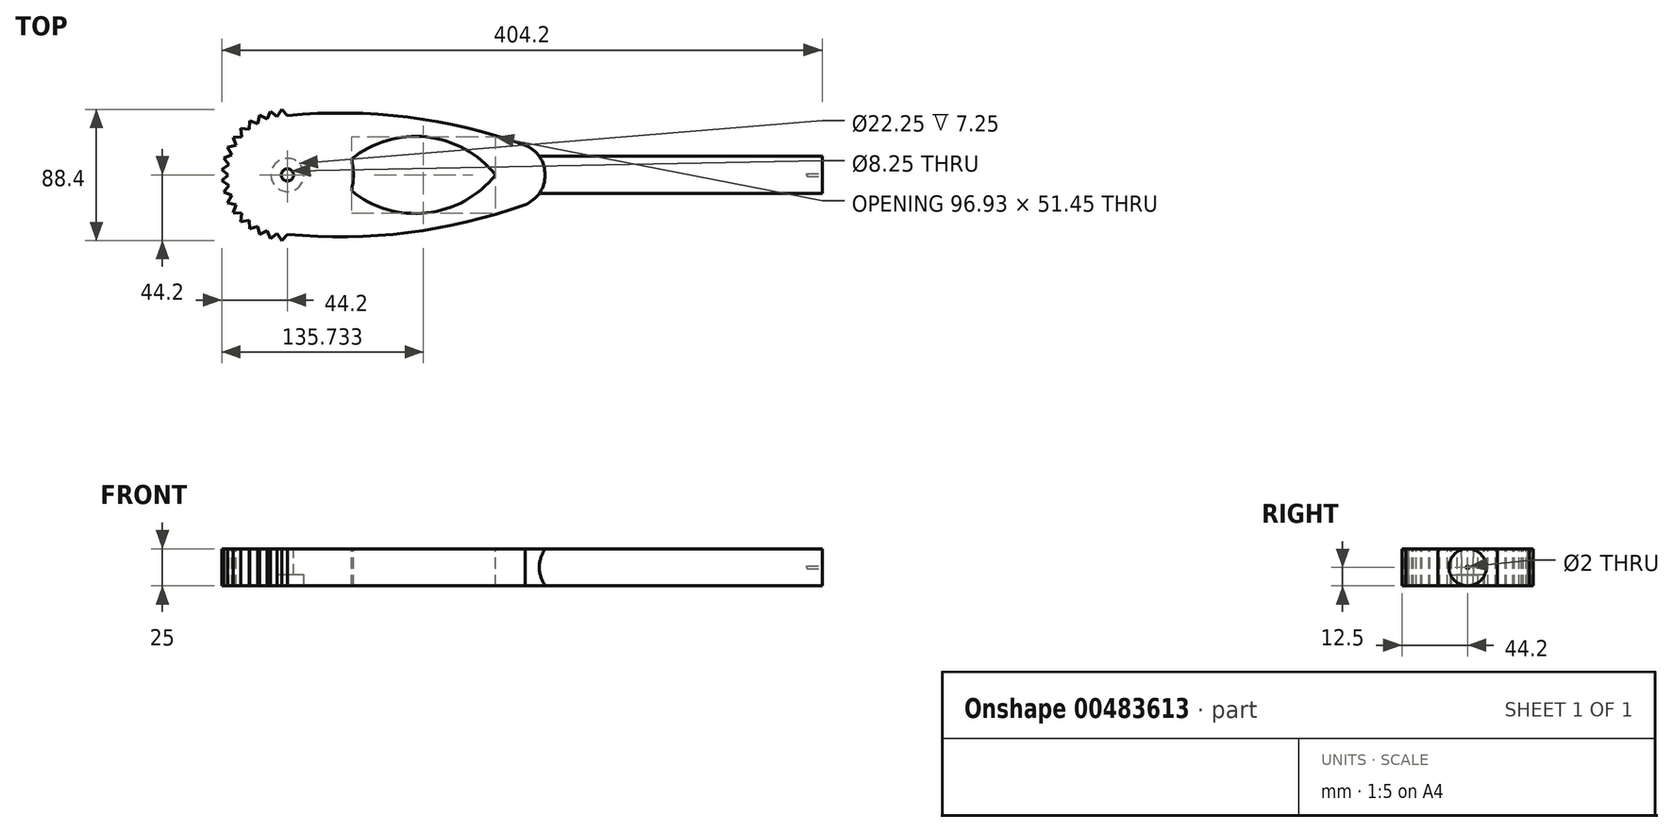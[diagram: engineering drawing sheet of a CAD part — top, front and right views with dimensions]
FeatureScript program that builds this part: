
annotation { "Feature Type Name" : "Feature", "Feature Type Description" : "" }
export const myFeature = defineFeature(function(context is Context, id is Id, definition is map)
    precondition{}
    {
        {
            var Q0;
            Q0=qCreatedBy(makeId("Top.planeOp"),FACE);
            var sketch = newSketch(context, id + "F0", { "sketchPlane" : qUnion([Q0])});
            skLineSegment(sketch, "E0.bottom", {"start": v(200, 12.5) * mm, "end": v(-200, 12.5) * mm});
            skLineSegment(sketch, "E0.top", {"start": v(200, -12.5) * mm, "end": v(-200, -12.5) * mm});
            skLineSegment(sketch, "E0.left", {"start": v(200, 12.5) * mm, "end": v(200, -12.5) * mm});
            skLineSegment(sketch, "E0.right", {"start": v(-200, 12.5) * mm, "end": v(-200, -12.5) * mm});
            skPoint(sketch, "E0.middle", {"position": v(0, 0) * mm});
            skPoint(sketch, "E1", {"position": v(-160, 0) * mm});
            skPoint(sketch, "E1.positionSnap0", {"position": v(-200, 0) * mm});
            skCircle(sketch, "E2", {"center": v(-160, 0) * mm, "radius": 40 * mm});
            skArc(sketch, "E3", {"start": v(0, 20) * mm, "mid": v(-78.9, 38.85) * mm, "end": v(-160, 40) * mm});
            skPoint(sketch, "E3.startSnap0", {"position": v(0, 12.5) * mm});
            skLineSegment(sketch, "E4", {"start": v(-200, 0) * mm, "end": v(200, 0) * mm});
            skArc(sketch, "E5.MirrorCS", {"start": v(0, -20) * mm, "mid": v(-78.9, -38.85) * mm, "end": v(-160, -40) * mm});
            skCircle(sketch, "E6", {"center": v(-8.16, 0) * mm, "radius": 21.6 * mm});
            skPoint(sketch, "E6.third.point", {"position": v(13.44, 0) * mm});
            skSolve(sketch);
        }
        {
            var Q0;
            {var subQ0=sQuery(id+"F0.wireOp",EDGE,"E0.left");Q0=makeQuery(id+"F0.imprint","IMPRINT",FACE,{"disambiguationData":[TD([[makeQuery(id+"F0.imprint","IMPRINT",EDGE,{"derivedFrom":subQ0}),-1.0]])]});}
            var Q1;
            {var subQ0=sQuery(id+"F0.wireOp",EDGE,"E2");var subQ1=sQuery(id+"F0.wireOp",EDGE,"E0.bottom");var subQ7=makeQuery(id+"F0.imprint","INTERSECT",VERTEX,{"disambiguationData":[OD(0.0)],"derivedFrom":[subQ1,subQ0]});Q1=makeQuery(id+"F0.imprint","IMPRINT",FACE,{"disambiguationData":[TD([[makeQuery(id+"F0.imprint","IMPRINT",EDGE,{"disambiguationData":[TD([[subQ7,-1.0]])],"derivedFrom":subQ1}),1.0]])]});}
            var Q2;
            {var subQ0=sQuery(id+"F0.wireOp",EDGE,"E2");var subQ4=sQuery(id+"F0.wireOp",EDGE,"E0.bottom");var subQ5=makeQuery(id+"F0.imprint","INTERSECT",VERTEX,{"disambiguationData":[OD(0.0)],"derivedFrom":[subQ4,subQ0]});Q2=makeQuery(id+"F0.imprint","IMPRINT",FACE,{"disambiguationData":[TD([[makeQuery(id+"F0.imprint","IMPRINT",EDGE,{"disambiguationData":[TD([[subQ5,1.0]])],"derivedFrom":subQ4}),1.0]])]});}
            var Q3;
            {var subQ0=sQuery(id+"F0.wireOp",EDGE,"E2");var subQ1=sQuery(id+"F0.wireOp",EDGE,"E0.bottom");var subQ2=makeQuery(id+"F0.imprint","INTERSECT",VERTEX,{"disambiguationData":[OD(0.0)],"derivedFrom":[subQ1,subQ0]});Q3=makeQuery(id+"F0.imprint","IMPRINT",FACE,{"disambiguationData":[TD([[makeQuery(id+"F0.imprint","IMPRINT",EDGE,{"disambiguationData":[TD([[subQ2,1.0]])],"derivedFrom":subQ1}),-1.0]])]});}
            var Q4;
            {var subQ0=sQuery(id+"F0.wireOp",EDGE,"E2");var subQ1=sQuery(id+"F0.wireOp",EDGE,"E0.top");var subQ2=makeQuery(id+"F0.imprint","INTERSECT",VERTEX,{"disambiguationData":[OD(0.0)],"derivedFrom":[subQ1,subQ0]});Q4=makeQuery(id+"F0.imprint","IMPRINT",FACE,{"disambiguationData":[TD([[makeQuery(id+"F0.imprint","IMPRINT",EDGE,{"disambiguationData":[TD([[subQ2,1.0]])],"derivedFrom":subQ1}),-1.0]])]});}
            var Q5;
            {var subQ0=sQuery(id+"F0.wireOp",EDGE,"E2");var subQ1=sQuery(id+"F0.wireOp",EDGE,"E0.top");var subQ2=makeQuery(id+"F0.imprint","INTERSECT",VERTEX,{"disambiguationData":[OD(0.0)],"derivedFrom":[subQ1,subQ0]});Q5=makeQuery(id+"F0.imprint","IMPRINT",FACE,{"disambiguationData":[TD([[makeQuery(id+"F0.imprint","IMPRINT",EDGE,{"disambiguationData":[TD([[subQ2,1.0]])],"derivedFrom":subQ1}),1.0]])]});}
            var Q6;
            {var subQ0=sQuery(id+"F0.wireOp",EDGE,"E6");var subQ1=sQuery(id+"F0.wireOp",EDGE,"E0.top");var subQ2=makeQuery(id+"F0.imprint","INTERSECT",VERTEX,{"disambiguationData":[OD(1.0)],"derivedFrom":[subQ1,subQ0]});Q6=makeQuery(id+"F0.imprint","IMPRINT",FACE,{"disambiguationData":[TD([[makeQuery(id+"F0.imprint","IMPRINT",EDGE,{"disambiguationData":[TD([[subQ2,-1.0]])],"derivedFrom":subQ1}),1.0]])]});}
            var Q7;
            {var subQ0=sQuery(id+"F0.wireOp",EDGE,"E6");var subQ1=sQuery(id+"F0.wireOp",EDGE,"E0.top");var subQ2=makeQuery(id+"F0.imprint","INTERSECT",VERTEX,{"disambiguationData":[OD(0.0)],"derivedFrom":[subQ1,subQ0]});Q7=makeQuery(id+"F0.imprint","IMPRINT",FACE,{"disambiguationData":[TD([[makeQuery(id+"F0.imprint","IMPRINT",EDGE,{"disambiguationData":[TD([[subQ2,-1.0]])],"derivedFrom":subQ1}),1.0]])]});}
            var Q8;
            {var subQ0=sQuery(id+"F0.wireOp",EDGE,"E6");var subQ1=sQuery(id+"F0.wireOp",EDGE,"E0.top");var subQ2=makeQuery(id+"F0.imprint","INTERSECT",VERTEX,{"disambiguationData":[OD(0.0)],"derivedFrom":[subQ1,subQ0]});Q8=makeQuery(id+"F0.imprint","IMPRINT",FACE,{"disambiguationData":[TD([[makeQuery(id+"F0.imprint","IMPRINT",EDGE,{"disambiguationData":[TD([[subQ2,-1.0]])],"derivedFrom":subQ1}),-1.0]])]});}
            var Q9;
            {var subQ0=sQuery(id+"F0.wireOp",EDGE,"E6");var subQ1=sQuery(id+"F0.wireOp",EDGE,"E0.top");var subQ2=makeQuery(id+"F0.imprint","INTERSECT",VERTEX,{"disambiguationData":[OD(1.0)],"derivedFrom":[subQ1,subQ0]});Q9=makeQuery(id+"F0.imprint","IMPRINT",FACE,{"disambiguationData":[TD([[makeQuery(id+"F0.imprint","IMPRINT",EDGE,{"disambiguationData":[TD([[subQ2,-1.0]])],"derivedFrom":subQ1}),-1.0]])]});}
            var Q10;
            {var subQ0=sQuery(id+"F0.wireOp",EDGE,"E6");var subQ1=sQuery(id+"F0.wireOp",EDGE,"E0.bottom");var subQ2=makeQuery(id+"F0.imprint","INTERSECT",VERTEX,{"disambiguationData":[OD(1.0)],"derivedFrom":[subQ1,subQ0]});Q10=makeQuery(id+"F0.imprint","IMPRINT",FACE,{"disambiguationData":[TD([[makeQuery(id+"F0.imprint","IMPRINT",EDGE,{"disambiguationData":[TD([[subQ2,-1.0]])],"derivedFrom":subQ1}),1.0]])]});}
            var Q11;
            {var subQ0=sQuery(id+"F0.wireOp",EDGE,"E6");var subQ1=sQuery(id+"F0.wireOp",EDGE,"E0.bottom");var subQ2=makeQuery(id+"F0.imprint","INTERSECT",VERTEX,{"disambiguationData":[OD(0.0)],"derivedFrom":[subQ1,subQ0]});Q11=makeQuery(id+"F0.imprint","IMPRINT",FACE,{"disambiguationData":[TD([[makeQuery(id+"F0.imprint","IMPRINT",EDGE,{"disambiguationData":[TD([[subQ2,-1.0]])],"derivedFrom":subQ1}),1.0]])]});}
            var Q12;
            {var subQ0=sQuery(id+"F0.wireOp",EDGE,"E6");var subQ1=sQuery(id+"F0.wireOp",EDGE,"E0.bottom");var subQ2=makeQuery(id+"F0.imprint","INTERSECT",VERTEX,{"disambiguationData":[OD(0.0)],"derivedFrom":[subQ1,subQ0]});Q12=makeQuery(id+"F0.imprint","IMPRINT",FACE,{"disambiguationData":[TD([[makeQuery(id+"F0.imprint","IMPRINT",EDGE,{"disambiguationData":[TD([[subQ2,-1.0]])],"derivedFrom":subQ1}),-1.0]])]});}
            var Q13;
            {var subQ0=sQuery(id+"F0.wireOp",EDGE,"E6");var subQ1=sQuery(id+"F0.wireOp",EDGE,"E0.bottom");var subQ2=makeQuery(id+"F0.imprint","INTERSECT",VERTEX,{"disambiguationData":[OD(1.0)],"derivedFrom":[subQ1,subQ0]});Q13=makeQuery(id+"F0.imprint","IMPRINT",FACE,{"disambiguationData":[TD([[makeQuery(id+"F0.imprint","IMPRINT",EDGE,{"disambiguationData":[TD([[subQ2,-1.0]])],"derivedFrom":subQ1}),-1.0]])]});}
            extrude(context, id + "F1", {"entities" : qUnion([Q0, Q1, Q2, Q3, Q4, Q5, Q6, Q7, Q8, Q9, Q10, Q11, Q12, Q13]), "depth" : 25 * mm});
        }
        {
            var Q0;
            Q0=makeQuery(id+"F1.opExtrude","CAP_EDGE",EDGE,{"disambiguationData":[OSD([sQuery(id+"F0.wireOp",EDGE,"E0.top")])],"isStart":false});
            var Q1;
            Q1=makeQuery(id+"F1.opExtrude","CAP_EDGE",EDGE,{"disambiguationData":[OSD([sQuery(id+"F0.wireOp",EDGE,"E0.bottom")])],"isStart":false});
            var Q2;
            Q2=makeQuery(id+"F1.opExtrude","CAP_EDGE",EDGE,{"disambiguationData":[OSD([sQuery(id+"F0.wireOp",EDGE,"E0.bottom")])],"isStart":true});
            var Q3;
            Q3=makeQuery(id+"F1.opExtrude","CAP_EDGE",EDGE,{"disambiguationData":[OSD([sQuery(id+"F0.wireOp",EDGE,"E0.top")])],"isStart":true});
            fillet(context, id + "F2", {"entities" : qUnion([Q0, Q1, Q2, Q3]), "radius" : 12.5 * mm, "tangentPropagation" : true, "allowEdgeOverflow" : false});
        }
        {
            var Q0;
            Q0=makeQuery(id+"F1.opExtrude","CAP_FACE",FACE,{"disambiguationData":[OSD([sQuery(id+"F0.wireOp",EDGE,"E0.bottom"),sQuery(id+"F0.wireOp",EDGE,"E0.top"),sQuery(id+"F0.wireOp",EDGE,"E0.left"),sQuery(id+"F0.wireOp",EDGE,"E0.right"),sQuery(id+"F0.wireOp",EDGE,"E2"),sQuery(id+"F0.wireOp",EDGE,"E3"),sQuery(id+"F0.wireOp",EDGE,"E5.MirrorCS"),sQuery(id+"F0.wireOp",EDGE,"E6")])],"isStart":false});
            var sketch = newSketch(context, id + "F3", { "sketchPlane" : qUnion([Q0])});
            skCircle(sketch, "E7", {"center": v(-160, 0) * mm, "radius": 40 * mm});
            skLineSegment(sketch, "E8", {"start": v(-160, 40) * mm, "end": v(-148.02, 53.01) * mm});
            skLineSegment(sketch, "E9", {"start": v(-171.98, 53.01) * mm, "end": v(-160, 40) * mm});
            skLineSegment(sketch, "E10.1.0", {"start": v(-166.95, 39.4) * mm, "end": v(-157.41, 54.29) * mm});
            skLineSegment(sketch, "E10.1.1", {"start": v(-181, 50.13) * mm, "end": v(-166.95, 39.4) * mm});
            skLineSegment(sketch, "E10.2.0", {"start": v(-173.68, 37.59) * mm, "end": v(-166.88, 53.91) * mm});
            skLineSegment(sketch, "E10.2.1", {"start": v(-189.38, 45.72) * mm, "end": v(-173.68, 37.59) * mm});
            skLineSegment(sketch, "E10.3.0", {"start": v(-180, 34.64) * mm, "end": v(-176.14, 51.9) * mm});
            skLineSegment(sketch, "E10.3.1", {"start": v(-196.88, 39.92) * mm, "end": v(-180, 34.64) * mm});
            skLineSegment(sketch, "E10.4.0", {"start": v(-185.71, 30.64) * mm, "end": v(-184.9, 48.3) * mm});
            skLineSegment(sketch, "E10.4.1", {"start": v(-203.25, 32.91) * mm, "end": v(-185.71, 30.64) * mm});
            skLineSegment(sketch, "E10.5.0", {"start": v(-190.64, 25.71) * mm, "end": v(-192.91, 43.25) * mm});
            skLineSegment(sketch, "E10.5.1", {"start": v(-208.3, 24.9) * mm, "end": v(-190.64, 25.71) * mm});
            skLineSegment(sketch, "E10.6.0", {"start": v(-194.64, 20) * mm, "end": v(-199.92, 36.88) * mm});
            skLineSegment(sketch, "E10.6.1", {"start": v(-211.9, 16.14) * mm, "end": v(-194.64, 20) * mm});
            skLineSegment(sketch, "E10.7.0", {"start": v(-197.59, 13.68) * mm, "end": v(-205.72, 29.38) * mm});
            skLineSegment(sketch, "E10.7.1", {"start": v(-213.91, 6.88) * mm, "end": v(-197.59, 13.68) * mm});
            skLineSegment(sketch, "E10.8.0", {"start": v(-199.4, 6.95) * mm, "end": v(-210.13, 21) * mm});
            skLineSegment(sketch, "E10.8.1", {"start": v(-214.29, -2.59) * mm, "end": v(-199.4, 6.95) * mm});
            skLineSegment(sketch, "E10.9.0", {"start": v(-200, 0) * mm, "end": v(-213.01, 11.98) * mm});
            skLineSegment(sketch, "E10.9.1", {"start": v(-213.01, -11.98) * mm, "end": v(-200, 0) * mm});
            skLineSegment(sketch, "E10.10.0", {"start": v(-199.4, -6.95) * mm, "end": v(-214.29, 2.59) * mm});
            skLineSegment(sketch, "E10.10.1", {"start": v(-210.13, -21) * mm, "end": v(-199.4, -6.95) * mm});
            skLineSegment(sketch, "E10.11.0", {"start": v(-197.59, -13.68) * mm, "end": v(-213.91, -6.88) * mm});
            skLineSegment(sketch, "E10.11.1", {"start": v(-205.72, -29.38) * mm, "end": v(-197.59, -13.68) * mm});
            skLineSegment(sketch, "E10.12.0", {"start": v(-194.64, -20) * mm, "end": v(-211.9, -16.14) * mm});
            skLineSegment(sketch, "E10.12.1", {"start": v(-199.92, -36.88) * mm, "end": v(-194.64, -20) * mm});
            skLineSegment(sketch, "E10.13.0", {"start": v(-190.64, -25.71) * mm, "end": v(-208.3, -24.9) * mm});
            skLineSegment(sketch, "E10.13.1", {"start": v(-192.91, -43.25) * mm, "end": v(-190.64, -25.71) * mm});
            skLineSegment(sketch, "E10.14.0", {"start": v(-185.71, -30.64) * mm, "end": v(-203.25, -32.91) * mm});
            skLineSegment(sketch, "E10.14.1", {"start": v(-184.9, -48.3) * mm, "end": v(-185.71, -30.64) * mm});
            skLineSegment(sketch, "E10.15.0", {"start": v(-180, -34.64) * mm, "end": v(-196.88, -39.92) * mm});
            skLineSegment(sketch, "E10.15.1", {"start": v(-176.14, -51.9) * mm, "end": v(-180, -34.64) * mm});
            skLineSegment(sketch, "E10.16.0", {"start": v(-173.68, -37.59) * mm, "end": v(-189.38, -45.72) * mm});
            skLineSegment(sketch, "E10.16.1", {"start": v(-166.88, -53.91) * mm, "end": v(-173.68, -37.59) * mm});
            skLineSegment(sketch, "E10.17.0", {"start": v(-166.95, -39.4) * mm, "end": v(-181, -50.13) * mm});
            skLineSegment(sketch, "E10.17.1", {"start": v(-157.41, -54.29) * mm, "end": v(-166.95, -39.4) * mm});
            skLineSegment(sketch, "E10.18.0", {"start": v(-160, -40) * mm, "end": v(-171.98, -53.01) * mm});
            skLineSegment(sketch, "E10.18.1", {"start": v(-148.02, -53.01) * mm, "end": v(-160, -40) * mm});
            skLineSegment(sketch, "E10.19.0", {"start": v(-153.05, -39.4) * mm, "end": v(-162.59, -54.29) * mm});
            skLineSegment(sketch, "E10.19.1", {"start": v(-139, -50.13) * mm, "end": v(-153.05, -39.4) * mm});
            skLineSegment(sketch, "E10.20.0", {"start": v(-146.32, -37.59) * mm, "end": v(-153.12, -53.91) * mm});
            skLineSegment(sketch, "E10.20.1", {"start": v(-130.62, -45.72) * mm, "end": v(-146.32, -37.59) * mm});
            skLineSegment(sketch, "E10.21.0", {"start": v(-140, -34.64) * mm, "end": v(-143.86, -51.9) * mm});
            skLineSegment(sketch, "E10.21.1", {"start": v(-123.12, -39.92) * mm, "end": v(-140, -34.64) * mm});
            skLineSegment(sketch, "E10.22.0", {"start": v(-134.29, -30.64) * mm, "end": v(-135.1, -48.3) * mm});
            skLineSegment(sketch, "E10.22.1", {"start": v(-116.75, -32.91) * mm, "end": v(-134.29, -30.64) * mm});
            skLineSegment(sketch, "E10.23.0", {"start": v(-129.36, -25.71) * mm, "end": v(-127.09, -43.25) * mm});
            skLineSegment(sketch, "E10.23.1", {"start": v(-111.7, -24.9) * mm, "end": v(-129.36, -25.71) * mm});
            skLineSegment(sketch, "E10.24.0", {"start": v(-125.36, -20) * mm, "end": v(-120.08, -36.88) * mm});
            skLineSegment(sketch, "E10.24.1", {"start": v(-108.1, -16.14) * mm, "end": v(-125.36, -20) * mm});
            skLineSegment(sketch, "E10.25.0", {"start": v(-122.41, -13.68) * mm, "end": v(-114.28, -29.38) * mm});
            skLineSegment(sketch, "E10.25.1", {"start": v(-106.09, -6.88) * mm, "end": v(-122.41, -13.68) * mm});
            skLineSegment(sketch, "E10.26.0", {"start": v(-120.6, -6.95) * mm, "end": v(-109.87, -21) * mm});
            skLineSegment(sketch, "E10.26.1", {"start": v(-105.71, 2.59) * mm, "end": v(-120.6, -6.95) * mm});
            skLineSegment(sketch, "E10.27.0", {"start": v(-120, 0) * mm, "end": v(-106.99, -11.98) * mm});
            skLineSegment(sketch, "E10.27.1", {"start": v(-106.99, 11.98) * mm, "end": v(-120, 0) * mm});
            skLineSegment(sketch, "E10.28.0", {"start": v(-120.6, 6.95) * mm, "end": v(-105.71, -2.59) * mm});
            skLineSegment(sketch, "E10.28.1", {"start": v(-109.87, 21) * mm, "end": v(-120.6, 6.95) * mm});
            skLineSegment(sketch, "E10.29.0", {"start": v(-122.41, 13.68) * mm, "end": v(-106.09, 6.88) * mm});
            skLineSegment(sketch, "E10.29.1", {"start": v(-114.28, 29.38) * mm, "end": v(-122.41, 13.68) * mm});
            skLineSegment(sketch, "E10.30.0", {"start": v(-125.36, 20) * mm, "end": v(-108.1, 16.14) * mm});
            skLineSegment(sketch, "E10.30.1", {"start": v(-120.08, 36.88) * mm, "end": v(-125.36, 20) * mm});
            skLineSegment(sketch, "E10.31.0", {"start": v(-129.36, 25.71) * mm, "end": v(-111.7, 24.9) * mm});
            skLineSegment(sketch, "E10.31.1", {"start": v(-127.09, 43.25) * mm, "end": v(-129.36, 25.71) * mm});
            skLineSegment(sketch, "E10.32.0", {"start": v(-134.29, 30.64) * mm, "end": v(-116.75, 32.91) * mm});
            skLineSegment(sketch, "E10.32.1", {"start": v(-135.1, 48.3) * mm, "end": v(-134.29, 30.64) * mm});
            skLineSegment(sketch, "E10.33.0", {"start": v(-140, 34.64) * mm, "end": v(-123.12, 39.92) * mm});
            skLineSegment(sketch, "E10.33.1", {"start": v(-143.86, 51.9) * mm, "end": v(-140, 34.64) * mm});
            skLineSegment(sketch, "E10.34.0", {"start": v(-146.32, 37.59) * mm, "end": v(-130.62, 45.72) * mm});
            skLineSegment(sketch, "E10.34.1", {"start": v(-153.12, 53.91) * mm, "end": v(-146.32, 37.59) * mm});
            skLineSegment(sketch, "E10.35.0", {"start": v(-153.05, 39.4) * mm, "end": v(-139, 50.13) * mm});
            skLineSegment(sketch, "E10.35.1", {"start": v(-162.59, 54.29) * mm, "end": v(-153.05, 39.4) * mm});
            skArc(sketch, "E11", {"start": v(-160, 70.8) * mm, "mid": v(-230.8, 0) * mm, "end": v(-160, -70.8) * mm});
            skLineSegment(sketch, "E12", {"start": v(-160, 70.8) * mm, "end": v(-160, -70.8) * mm});
            skPoint(sketch, "E13.orphan", {"position": v(-160, 103.77) * mm});
            skSolve(sketch);
        }
        {
            var Q0;
            {var subQ8=sQuery(id+"F3.wireOp",EDGE,"E12");var subQ17=sQuery(id+"F3.wireOp",EDGE,"E11");var subQ18=makeQuery(id+"F3.imprint","INTERSECT",VERTEX,{"disambiguationData":[OD(0.0)],"derivedFrom":[subQ17,subQ8]});Q0=makeQuery(id+"F3.imprint","IMPRINT",FACE,{"disambiguationData":[TD([[makeQuery(id+"F3.imprint","IMPRINT",EDGE,{"disambiguationData":[TD([[subQ18,-1.0]])],"derivedFrom":subQ17}),1.0]])]});}
            var Q1;
            {var subQ0=sQuery(id+"F3.wireOp",EDGE,"E10.7.1");var subQ3=sQuery(id+"F3.wireOp",EDGE,"E10.8.0");var subQ5=makeQuery(id+"F3.imprint","INTERSECT",VERTEX,{"derivedFrom":[subQ0,subQ3]});Q1=makeQuery(id+"F3.imprint","IMPRINT",FACE,{"disambiguationData":[TD([[makeQuery(id+"F3.imprint","IMPRINT",EDGE,{"disambiguationData":[TD([[subQ5,-1.0]])],"derivedFrom":subQ0}),-1.0]])]});}
            var Q2;
            {var subQ0=sQuery(id+"F3.wireOp",EDGE,"E10.9.0");var subQ3=sQuery(id+"F3.wireOp",EDGE,"E10.8.1");var subQ5=makeQuery(id+"F3.imprint","INTERSECT",VERTEX,{"derivedFrom":[subQ3,subQ0]});Q2=makeQuery(id+"F3.imprint","IMPRINT",FACE,{"disambiguationData":[TD([[makeQuery(id+"F3.imprint","IMPRINT",EDGE,{"disambiguationData":[TD([[subQ5,-1.0]])],"derivedFrom":subQ3}),-1.0]])]});}
            var Q3;
            {var subQ0=sQuery(id+"F3.wireOp",EDGE,"E10.9.1");var subQ3=sQuery(id+"F3.wireOp",EDGE,"E10.10.0");var subQ5=makeQuery(id+"F3.imprint","INTERSECT",VERTEX,{"derivedFrom":[subQ0,subQ3]});Q3=makeQuery(id+"F3.imprint","IMPRINT",FACE,{"disambiguationData":[TD([[makeQuery(id+"F3.imprint","IMPRINT",EDGE,{"disambiguationData":[TD([[subQ5,-1.0]])],"derivedFrom":subQ0}),-1.0]])]});}
            var Q4;
            {var subQ0=sQuery(id+"F3.wireOp",EDGE,"E10.10.1");var subQ3=sQuery(id+"F3.wireOp",EDGE,"E10.11.0");var subQ5=makeQuery(id+"F3.imprint","INTERSECT",VERTEX,{"derivedFrom":[subQ0,subQ3]});Q4=makeQuery(id+"F3.imprint","IMPRINT",FACE,{"disambiguationData":[TD([[makeQuery(id+"F3.imprint","IMPRINT",EDGE,{"disambiguationData":[TD([[subQ5,-1.0]])],"derivedFrom":subQ0}),-1.0]])]});}
            var Q5;
            {var subQ0=sQuery(id+"F3.wireOp",EDGE,"E10.8.0");var subQ1=sQuery(id+"F3.wireOp",EDGE,"E10.6.1");var subQ2=makeQuery(id+"F3.imprint","INTERSECT",VERTEX,{"derivedFrom":[subQ1,subQ0]});Q5=makeQuery(id+"F3.imprint","IMPRINT",FACE,{"disambiguationData":[TD([[makeQuery(id+"F3.imprint","IMPRINT",EDGE,{"disambiguationData":[TD([[subQ2,-1.0]])],"derivedFrom":subQ1}),-1.0]])]});}
            var Q6;
            {var subQ0=sQuery(id+"F3.wireOp",EDGE,"E10.9.0");var subQ1=sQuery(id+"F3.wireOp",EDGE,"E10.7.1");var subQ2=makeQuery(id+"F3.imprint","INTERSECT",VERTEX,{"derivedFrom":[subQ1,subQ0]});Q6=makeQuery(id+"F3.imprint","IMPRINT",FACE,{"disambiguationData":[TD([[makeQuery(id+"F3.imprint","IMPRINT",EDGE,{"disambiguationData":[TD([[subQ2,-1.0]])],"derivedFrom":subQ1}),-1.0]])]});}
            var Q7;
            {var subQ0=sQuery(id+"F3.wireOp",EDGE,"E10.6.1");var subQ3=sQuery(id+"F3.wireOp",EDGE,"E10.7.0");var subQ5=makeQuery(id+"F3.imprint","INTERSECT",VERTEX,{"derivedFrom":[subQ0,subQ3]});Q7=makeQuery(id+"F3.imprint","IMPRINT",FACE,{"disambiguationData":[TD([[makeQuery(id+"F3.imprint","IMPRINT",EDGE,{"disambiguationData":[TD([[subQ5,-1.0]])],"derivedFrom":subQ0}),-1.0]])]});}
            var Q8;
            {var subQ0=sQuery(id+"F3.wireOp",EDGE,"E10.11.1");var subQ3=sQuery(id+"F3.wireOp",EDGE,"E10.12.0");var subQ5=makeQuery(id+"F3.imprint","INTERSECT",VERTEX,{"derivedFrom":[subQ0,subQ3]});Q8=makeQuery(id+"F3.imprint","IMPRINT",FACE,{"disambiguationData":[TD([[makeQuery(id+"F3.imprint","IMPRINT",EDGE,{"disambiguationData":[TD([[subQ5,-1.0]])],"derivedFrom":subQ0}),-1.0]])]});}
            extrude(context, id + "F4", {"entities" : qUnion([Q0, Q1, Q2, Q3, Q4, Q5, Q6, Q7, Q8]), "operationType" : NewBodyOperationType.REMOVE, "endBound" : BoundingType.THROUGH_ALL, "oppositeDirection" : true, "depth" : 25 * mm});
        }
        {
            var Q0;
            Q0=makeQuery(id+"F1.opExtrude","CAP_FACE",FACE,{"disambiguationData":[OSD([sQuery(id+"F0.wireOp",EDGE,"E0.bottom"),sQuery(id+"F0.wireOp",EDGE,"E0.top"),sQuery(id+"F0.wireOp",EDGE,"E0.left"),sQuery(id+"F0.wireOp",EDGE,"E0.right"),sQuery(id+"F0.wireOp",EDGE,"E2"),sQuery(id+"F0.wireOp",EDGE,"E3"),sQuery(id+"F0.wireOp",EDGE,"E5.MirrorCS"),sQuery(id+"F0.wireOp",EDGE,"E6")])],"isStart":false});
            var sketch = newSketch(context, id + "F5", { "sketchPlane" : qUnion([Q0])});
            skCircle(sketch, "E14", {"center": v(-160, 0) * mm, "radius": 4.12 * mm});
            skCircle(sketch, "E15", {"center": v(-160, 0) * mm, "radius": 11.12 * mm});
            skSolve(sketch);
        }
        {
            var Q0;
            Q0=makeQuery(id+"F5.imprint","IMPRINT",FACE,{"disambiguationData":[TD([[makeQuery(id+"F5.imprint","IMPRINT",EDGE,{"derivedFrom":sQuery(id+"F5.wireOp",EDGE,"E14")}),-1.0]])]});
            var Q1;
            Q1=makeQuery(id+"F5.imprint","IMPRINT",FACE,{"disambiguationData":[TD([[makeQuery(id+"F5.imprint","IMPRINT",EDGE,{"derivedFrom":sQuery(id+"F5.wireOp",EDGE,"E14")}),1.0]])]});
            extrude(context, id + "F6", {"entities" : qUnion([Q0, Q1]), "operationType" : NewBodyOperationType.REMOVE, "oppositeDirection" : true, "depth" : 25 * mm});
        }
        {
            var Q0;
            {var subQ0=sQuery(id+"F3.wireOp",EDGE,"E9");var subQ3=sQuery(id+"F3.wireOp",EDGE,"E10.1.0");var subQ5=makeQuery(id+"F3.imprint","INTERSECT",VERTEX,{"derivedFrom":[subQ0,subQ3]});Q0=makeQuery(id+"F3.imprint","IMPRINT",FACE,{"disambiguationData":[TD([[makeQuery(id+"F3.imprint","IMPRINT",EDGE,{"disambiguationData":[TD([[subQ5,1.0]])],"derivedFrom":subQ3}),-1.0]])]});}
            var Q1;
            {var subQ0=sQuery(id+"F3.wireOp",EDGE,"E10.1.1");var subQ3=sQuery(id+"F3.wireOp",EDGE,"E10.2.0");var subQ5=makeQuery(id+"F3.imprint","INTERSECT",VERTEX,{"derivedFrom":[subQ0,subQ3]});Q1=makeQuery(id+"F3.imprint","IMPRINT",FACE,{"disambiguationData":[TD([[makeQuery(id+"F3.imprint","IMPRINT",EDGE,{"disambiguationData":[TD([[subQ5,-1.0]])],"derivedFrom":subQ0}),-1.0]])]});}
            var Q2;
            {var subQ0=sQuery(id+"F3.wireOp",EDGE,"E10.2.1");var subQ3=sQuery(id+"F3.wireOp",EDGE,"E10.3.0");var subQ5=makeQuery(id+"F3.imprint","INTERSECT",VERTEX,{"derivedFrom":[subQ0,subQ3]});Q2=makeQuery(id+"F3.imprint","IMPRINT",FACE,{"disambiguationData":[TD([[makeQuery(id+"F3.imprint","IMPRINT",EDGE,{"disambiguationData":[TD([[subQ5,-1.0]])],"derivedFrom":subQ0}),-1.0]])]});}
            var Q3;
            {var subQ0=sQuery(id+"F3.wireOp",EDGE,"E10.3.1");var subQ3=sQuery(id+"F3.wireOp",EDGE,"E10.4.0");var subQ5=makeQuery(id+"F3.imprint","INTERSECT",VERTEX,{"derivedFrom":[subQ0,subQ3]});Q3=makeQuery(id+"F3.imprint","IMPRINT",FACE,{"disambiguationData":[TD([[makeQuery(id+"F3.imprint","IMPRINT",EDGE,{"disambiguationData":[TD([[subQ5,-1.0]])],"derivedFrom":subQ0}),-1.0]])]});}
            var Q4;
            {var subQ0=sQuery(id+"F3.wireOp",EDGE,"E10.4.1");var subQ3=sQuery(id+"F3.wireOp",EDGE,"E10.5.0");var subQ5=makeQuery(id+"F3.imprint","INTERSECT",VERTEX,{"derivedFrom":[subQ0,subQ3]});Q4=makeQuery(id+"F3.imprint","IMPRINT",FACE,{"disambiguationData":[TD([[makeQuery(id+"F3.imprint","IMPRINT",EDGE,{"disambiguationData":[TD([[subQ5,-1.0]])],"derivedFrom":subQ0}),-1.0]])]});}
            var Q5;
            {var subQ0=sQuery(id+"F3.wireOp",EDGE,"E10.5.1");var subQ3=sQuery(id+"F3.wireOp",EDGE,"E10.6.0");var subQ5=makeQuery(id+"F3.imprint","INTERSECT",VERTEX,{"derivedFrom":[subQ0,subQ3]});Q5=makeQuery(id+"F3.imprint","IMPRINT",FACE,{"disambiguationData":[TD([[makeQuery(id+"F3.imprint","IMPRINT",EDGE,{"disambiguationData":[TD([[subQ5,-1.0]])],"derivedFrom":subQ0}),-1.0]])]});}
            var Q6;
            {var subQ0=sQuery(id+"F3.wireOp",EDGE,"E10.6.1");var subQ3=sQuery(id+"F3.wireOp",EDGE,"E10.7.0");var subQ5=makeQuery(id+"F3.imprint","INTERSECT",VERTEX,{"derivedFrom":[subQ0,subQ3]});Q6=makeQuery(id+"F3.imprint","IMPRINT",FACE,{"disambiguationData":[TD([[makeQuery(id+"F3.imprint","IMPRINT",EDGE,{"disambiguationData":[TD([[subQ5,-1.0]])],"derivedFrom":subQ0}),-1.0]])]});}
            var Q7;
            {var subQ0=sQuery(id+"F3.wireOp",EDGE,"E10.7.1");var subQ3=sQuery(id+"F3.wireOp",EDGE,"E10.8.0");var subQ5=makeQuery(id+"F3.imprint","INTERSECT",VERTEX,{"derivedFrom":[subQ0,subQ3]});Q7=makeQuery(id+"F3.imprint","IMPRINT",FACE,{"disambiguationData":[TD([[makeQuery(id+"F3.imprint","IMPRINT",EDGE,{"disambiguationData":[TD([[subQ5,-1.0]])],"derivedFrom":subQ0}),-1.0]])]});}
            var Q8;
            {var subQ0=sQuery(id+"F3.wireOp",EDGE,"E10.9.0");var subQ3=sQuery(id+"F3.wireOp",EDGE,"E10.8.1");var subQ5=makeQuery(id+"F3.imprint","INTERSECT",VERTEX,{"derivedFrom":[subQ3,subQ0]});Q8=makeQuery(id+"F3.imprint","IMPRINT",FACE,{"disambiguationData":[TD([[makeQuery(id+"F3.imprint","IMPRINT",EDGE,{"disambiguationData":[TD([[subQ5,-1.0]])],"derivedFrom":subQ3}),-1.0]])]});}
            var Q9;
            {var subQ0=sQuery(id+"F3.wireOp",EDGE,"E10.9.1");var subQ3=sQuery(id+"F3.wireOp",EDGE,"E10.10.0");var subQ5=makeQuery(id+"F3.imprint","INTERSECT",VERTEX,{"derivedFrom":[subQ0,subQ3]});Q9=makeQuery(id+"F3.imprint","IMPRINT",FACE,{"disambiguationData":[TD([[makeQuery(id+"F3.imprint","IMPRINT",EDGE,{"disambiguationData":[TD([[subQ5,-1.0]])],"derivedFrom":subQ0}),-1.0]])]});}
            var Q10;
            {var subQ0=sQuery(id+"F3.wireOp",EDGE,"E10.10.1");var subQ3=sQuery(id+"F3.wireOp",EDGE,"E10.11.0");var subQ5=makeQuery(id+"F3.imprint","INTERSECT",VERTEX,{"derivedFrom":[subQ0,subQ3]});Q10=makeQuery(id+"F3.imprint","IMPRINT",FACE,{"disambiguationData":[TD([[makeQuery(id+"F3.imprint","IMPRINT",EDGE,{"disambiguationData":[TD([[subQ5,-1.0]])],"derivedFrom":subQ0}),-1.0]])]});}
            var Q11;
            {var subQ0=sQuery(id+"F3.wireOp",EDGE,"E10.13.1");var subQ3=sQuery(id+"F3.wireOp",EDGE,"E10.14.0");var subQ5=makeQuery(id+"F3.imprint","INTERSECT",VERTEX,{"derivedFrom":[subQ0,subQ3]});Q11=makeQuery(id+"F3.imprint","IMPRINT",FACE,{"disambiguationData":[TD([[makeQuery(id+"F3.imprint","IMPRINT",EDGE,{"disambiguationData":[TD([[subQ5,-1.0]])],"derivedFrom":subQ0}),-1.0]])]});}
            var Q12;
            {var subQ0=sQuery(id+"F3.wireOp",EDGE,"E10.14.1");var subQ3=sQuery(id+"F3.wireOp",EDGE,"E10.15.0");var subQ5=makeQuery(id+"F3.imprint","INTERSECT",VERTEX,{"derivedFrom":[subQ0,subQ3]});Q12=makeQuery(id+"F3.imprint","IMPRINT",FACE,{"disambiguationData":[TD([[makeQuery(id+"F3.imprint","IMPRINT",EDGE,{"disambiguationData":[TD([[subQ5,-1.0]])],"derivedFrom":subQ0}),-1.0]])]});}
            var Q13;
            {var subQ0=sQuery(id+"F3.wireOp",EDGE,"E10.15.1");var subQ3=sQuery(id+"F3.wireOp",EDGE,"E10.16.0");var subQ5=makeQuery(id+"F3.imprint","INTERSECT",VERTEX,{"derivedFrom":[subQ0,subQ3]});Q13=makeQuery(id+"F3.imprint","IMPRINT",FACE,{"disambiguationData":[TD([[makeQuery(id+"F3.imprint","IMPRINT",EDGE,{"disambiguationData":[TD([[subQ5,-1.0]])],"derivedFrom":subQ0}),-1.0]])]});}
            var Q14;
            {var subQ0=sQuery(id+"F3.wireOp",EDGE,"E10.12.1");var subQ3=sQuery(id+"F3.wireOp",EDGE,"E10.13.0");var subQ5=makeQuery(id+"F3.imprint","INTERSECT",VERTEX,{"derivedFrom":[subQ0,subQ3]});Q14=makeQuery(id+"F3.imprint","IMPRINT",FACE,{"disambiguationData":[TD([[makeQuery(id+"F3.imprint","IMPRINT",EDGE,{"disambiguationData":[TD([[subQ5,-1.0]])],"derivedFrom":subQ0}),-1.0]])]});}
            var Q15;
            {var subQ0=sQuery(id+"F3.wireOp",EDGE,"E10.11.1");var subQ3=sQuery(id+"F3.wireOp",EDGE,"E10.12.0");var subQ5=makeQuery(id+"F3.imprint","INTERSECT",VERTEX,{"derivedFrom":[subQ0,subQ3]});Q15=makeQuery(id+"F3.imprint","IMPRINT",FACE,{"disambiguationData":[TD([[makeQuery(id+"F3.imprint","IMPRINT",EDGE,{"disambiguationData":[TD([[subQ5,-1.0]])],"derivedFrom":subQ0}),-1.0]])]});}
            var Q16;
            {var subQ0=sQuery(id+"F3.wireOp",EDGE,"E10.16.1");var subQ3=sQuery(id+"F3.wireOp",EDGE,"E10.17.0");var subQ5=makeQuery(id+"F3.imprint","INTERSECT",VERTEX,{"derivedFrom":[subQ0,subQ3]});Q16=makeQuery(id+"F3.imprint","IMPRINT",FACE,{"disambiguationData":[TD([[makeQuery(id+"F3.imprint","IMPRINT",EDGE,{"disambiguationData":[TD([[subQ5,-1.0]])],"derivedFrom":subQ0}),-1.0]])]});}
            var Q17;
            {var subQ0=sQuery(id+"F3.wireOp",EDGE,"E10.18.0");var subQ3=sQuery(id+"F3.wireOp",EDGE,"E10.17.1");var subQ5=makeQuery(id+"F3.imprint","INTERSECT",VERTEX,{"derivedFrom":[subQ3,subQ0]});Q17=makeQuery(id+"F3.imprint","IMPRINT",FACE,{"disambiguationData":[TD([[makeQuery(id+"F3.imprint","IMPRINT",EDGE,{"disambiguationData":[TD([[subQ5,-1.0]])],"derivedFrom":subQ3}),-1.0]])]});}
            extrude(context, id + "F7", {"entities" : qUnion([Q0, Q1, Q2, Q3, Q4, Q5, Q6, Q7, Q8, Q9, Q10, Q11, Q12, Q13, Q14, Q15, Q16, Q17]), "operationType" : NewBodyOperationType.ADD, "oppositeDirection" : true, "depth" : 25 * mm});
        }
        {
            var Q0;
            Q0=makeQuery(id+"F5.imprint","IMPRINT",FACE,{"disambiguationData":[TD([[makeQuery(id+"F5.imprint","IMPRINT",EDGE,{"derivedFrom":sQuery(id+"F5.wireOp",EDGE,"E14")}),-1.0]])]});
            extrude(context, id + "F8", {"entities" : qUnion([Q0]), "operationType" : NewBodyOperationType.ADD, "oppositeDirection" : true, "depth" : 17.75 * mm});
        }
        {
            var Q0;
            Q0=makeQuery(id+"F1.opExtrude","SWEPT_FACE",FACE,{"disambiguationData":[OSD([sQuery(id+"F0.wireOp",EDGE,"E0.left")])]});
            var sketch = newSketch(context, id + "F9", { "sketchPlane" : qUnion([Q0])});
            skPoint(sketch, "E16", {"position": v(0, 12.5) * mm});
            skSolve(sketch);
        }
        {
            var Q0;
            Q0=sQuery(id+"F9.wireOp",VERTEX,"E16");
            var Q1;
            Q1=makeQuery(id+"F1.opExtrude","SWEPT_BODY",BODY,{"disambiguationData":[OSD([sQuery(id+"F0.wireOp",EDGE,"E0.bottom"),sQuery(id+"F0.wireOp",EDGE,"E0.top"),sQuery(id+"F0.wireOp",EDGE,"E0.left"),sQuery(id+"F0.wireOp",EDGE,"E0.right"),sQuery(id+"F0.wireOp",EDGE,"E2"),sQuery(id+"F0.wireOp",EDGE,"E3"),sQuery(id+"F0.wireOp",EDGE,"E5.MirrorCS"),sQuery(id+"F0.wireOp",EDGE,"E6")])]});
            hole(context, id + "F10", {"style" : HoleStyle.SIMPLE, "endStyle" : HoleEndStyle.BLIND, "holeDiameter" : 2 * mm, "holeDepth" : 10 * mm, "isTappedThrough" : true, "tappedDepth" : 12 * mm, "tapClearance" : 3, "locations" : qUnion([Q0]), "scope" : qUnion([Q1])});
        }
        {
            var Q0;
            {var subQ0=sQuery(id+"F3.wireOp",EDGE,"E7");Q0=makeQuery(id+"F8.boolean.opBoolean","MERGE",FACE,{"derivedFrom":[makeQuery(id+"F7.boolean.opBoolean","MERGE",FACE,{"derivedFrom":[makeQuery(id+"F1.opExtrude","CAP_FACE",FACE,{"disambiguationData":[OSD([sQuery(id+"F0.wireOp",EDGE,"E0.bottom"),sQuery(id+"F0.wireOp",EDGE,"E0.top"),sQuery(id+"F0.wireOp",EDGE,"E0.left"),sQuery(id+"F0.wireOp",EDGE,"E0.right"),sQuery(id+"F0.wireOp",EDGE,"E2"),sQuery(id+"F0.wireOp",EDGE,"E3"),sQuery(id+"F0.wireOp",EDGE,"E5.MirrorCS"),sQuery(id+"F0.wireOp",EDGE,"E6")])],"isStart":false}),makeQuery(id+"F7.opExtrude","CAP_FACE",FACE,{"disambiguationData":[OSD([subQ0,sQuery(id+"F3.wireOp",EDGE,"E9"),sQuery(id+"F3.wireOp",EDGE,"E10.1.0")])],"isStart":true}),makeQuery(id+"F7.opExtrude","CAP_FACE",FACE,{"disambiguationData":[OSD([subQ0,sQuery(id+"F3.wireOp",EDGE,"E10.1.1"),sQuery(id+"F3.wireOp",EDGE,"E10.2.0")])],"isStart":true}),makeQuery(id+"F7.opExtrude","CAP_FACE",FACE,{"disambiguationData":[OSD([subQ0,sQuery(id+"F3.wireOp",EDGE,"E10.2.1"),sQuery(id+"F3.wireOp",EDGE,"E10.3.0")])],"isStart":true}),makeQuery(id+"F7.opExtrude","CAP_FACE",FACE,{"disambiguationData":[OSD([subQ0,sQuery(id+"F3.wireOp",EDGE,"E10.3.1"),sQuery(id+"F3.wireOp",EDGE,"E10.4.0")])],"isStart":true}),makeQuery(id+"F7.opExtrude","CAP_FACE",FACE,{"disambiguationData":[OSD([subQ0,sQuery(id+"F3.wireOp",EDGE,"E10.4.1"),sQuery(id+"F3.wireOp",EDGE,"E10.5.0")])],"isStart":true}),makeQuery(id+"F7.opExtrude","CAP_FACE",FACE,{"disambiguationData":[OSD([subQ0,sQuery(id+"F3.wireOp",EDGE,"E10.5.1"),sQuery(id+"F3.wireOp",EDGE,"E10.6.0")])],"isStart":true}),makeQuery(id+"F7.opExtrude","CAP_FACE",FACE,{"disambiguationData":[OSD([subQ0,sQuery(id+"F3.wireOp",EDGE,"E10.6.1"),sQuery(id+"F3.wireOp",EDGE,"E10.7.0")])],"isStart":true}),makeQuery(id+"F7.opExtrude","CAP_FACE",FACE,{"disambiguationData":[OSD([subQ0,sQuery(id+"F3.wireOp",EDGE,"E10.7.1"),sQuery(id+"F3.wireOp",EDGE,"E10.8.0")])],"isStart":true}),makeQuery(id+"F7.opExtrude","CAP_FACE",FACE,{"disambiguationData":[OSD([subQ0,sQuery(id+"F3.wireOp",EDGE,"E10.8.1"),sQuery(id+"F3.wireOp",EDGE,"E10.9.0")])],"isStart":true}),makeQuery(id+"F7.opExtrude","CAP_FACE",FACE,{"disambiguationData":[OSD([subQ0,sQuery(id+"F3.wireOp",EDGE,"E10.9.1"),sQuery(id+"F3.wireOp",EDGE,"E10.10.0")])],"isStart":true}),makeQuery(id+"F7.opExtrude","CAP_FACE",FACE,{"disambiguationData":[OSD([subQ0,sQuery(id+"F3.wireOp",EDGE,"E10.10.1"),sQuery(id+"F3.wireOp",EDGE,"E10.11.0")])],"isStart":true}),makeQuery(id+"F7.opExtrude","CAP_FACE",FACE,{"disambiguationData":[OSD([subQ0,sQuery(id+"F3.wireOp",EDGE,"E10.11.1"),sQuery(id+"F3.wireOp",EDGE,"E10.12.0")])],"isStart":true}),makeQuery(id+"F7.opExtrude","CAP_FACE",FACE,{"disambiguationData":[OSD([subQ0,sQuery(id+"F3.wireOp",EDGE,"E10.12.1"),sQuery(id+"F3.wireOp",EDGE,"E10.13.0")])],"isStart":true}),makeQuery(id+"F7.opExtrude","CAP_FACE",FACE,{"disambiguationData":[OSD([subQ0,sQuery(id+"F3.wireOp",EDGE,"E10.13.1"),sQuery(id+"F3.wireOp",EDGE,"E10.14.0")])],"isStart":true}),makeQuery(id+"F7.opExtrude","CAP_FACE",FACE,{"disambiguationData":[OSD([subQ0,sQuery(id+"F3.wireOp",EDGE,"E10.14.1"),sQuery(id+"F3.wireOp",EDGE,"E10.15.0")])],"isStart":true}),makeQuery(id+"F7.opExtrude","CAP_FACE",FACE,{"disambiguationData":[OSD([subQ0,sQuery(id+"F3.wireOp",EDGE,"E10.15.1"),sQuery(id+"F3.wireOp",EDGE,"E10.16.0")])],"isStart":true}),makeQuery(id+"F7.opExtrude","CAP_FACE",FACE,{"disambiguationData":[OSD([subQ0,sQuery(id+"F3.wireOp",EDGE,"E10.16.1"),sQuery(id+"F3.wireOp",EDGE,"E10.17.0")])],"isStart":true}),makeQuery(id+"F7.opExtrude","CAP_FACE",FACE,{"disambiguationData":[OSD([subQ0,sQuery(id+"F3.wireOp",EDGE,"E10.17.1"),sQuery(id+"F3.wireOp",EDGE,"E10.18.0")])],"isStart":true})]}),makeQuery(id+"F8.opExtrude","CAP_FACE",FACE,{"disambiguationData":[OSD([sQuery(id+"F5.wireOp",EDGE,"E14"),sQuery(id+"F5.wireOp",EDGE,"E15")])],"isStart":true})]});}
            var sketch = newSketch(context, id + "F11", { "sketchPlane" : qUnion([Q0])});
            skCircle(sketch, "E17", {"center": v(-160, 0) * mm, "radius": 40 * mm});
            skCircle(sketch, "E18", {"center": v(-160, 0) * mm, "radius": 44.37 * mm});
            skCircle(sketch, "E19", {"center": v(0, 0) * mm, "radius": 20 * mm});
            skCircle(sketch, "E20", {"center": v(-20, 0) * mm, "radius": 20 * mm});
            skCircle(sketch, "E21", {"center": v(-115.63, 0) * mm, "radius": 44.37 * mm});
            skArc(sketch, "E22", {"start": v(-141.97, 35.7) * mm, "mid": v(-83.2, -25.33) * mm, "end": v(-10, 17.32) * mm});
            skArc(sketch, "E23", {"start": v(-10, -17.32) * mm, "mid": v(-83.2, 25.33) * mm, "end": v(-141.97, -35.7) * mm});
            skSolve(sketch);
        }
        {
            var Q0;
            {var subQ0=sQuery(id+"F11.wireOp",EDGE,"E23");var subQ1=sQuery(id+"F11.wireOp",EDGE,"E18");var subQ2=makeQuery(id+"F11.imprint","INTERSECT",VERTEX,{"derivedFrom":[subQ1,subQ0]});Q0=makeQuery(id+"F11.imprint","IMPRINT",FACE,{"disambiguationData":[TD([[makeQuery(id+"F11.imprint","IMPRINT",EDGE,{"disambiguationData":[TD([[subQ2,1.0]])],"derivedFrom":subQ1}),-1.0]])]});}
            var Q1;
            {var subQ0=sQuery(id+"F11.wireOp",EDGE,"E23");var subQ1=sQuery(id+"F11.wireOp",EDGE,"E20");var subQ2=makeQuery(id+"F11.imprint","INTERSECT",VERTEX,{"derivedFrom":[subQ1,subQ0]});Q1=makeQuery(id+"F11.imprint","IMPRINT",FACE,{"disambiguationData":[TD([[makeQuery(id+"F11.imprint","IMPRINT",EDGE,{"disambiguationData":[TD([[subQ2,-1.0]])],"derivedFrom":subQ1}),1.0]])]});}
            var Q2;
            {var subQ0=sQuery(id+"F11.wireOp",EDGE,"E23");var subQ1=sQuery(id+"F11.wireOp",EDGE,"E20");var subQ2=makeQuery(id+"F11.imprint","INTERSECT",VERTEX,{"derivedFrom":[subQ1,subQ0]});Q2=makeQuery(id+"F11.imprint","IMPRINT",FACE,{"disambiguationData":[TD([[makeQuery(id+"F11.imprint","IMPRINT",EDGE,{"disambiguationData":[TD([[subQ2,-1.0]])],"derivedFrom":subQ1}),-1.0]])]});}
            extrude(context, id + "F12", {"entities" : qUnion([Q0, Q1, Q2]), "operationType" : NewBodyOperationType.REMOVE, "oppositeDirection" : true, "depth" : 25 * mm});
        }
    });
